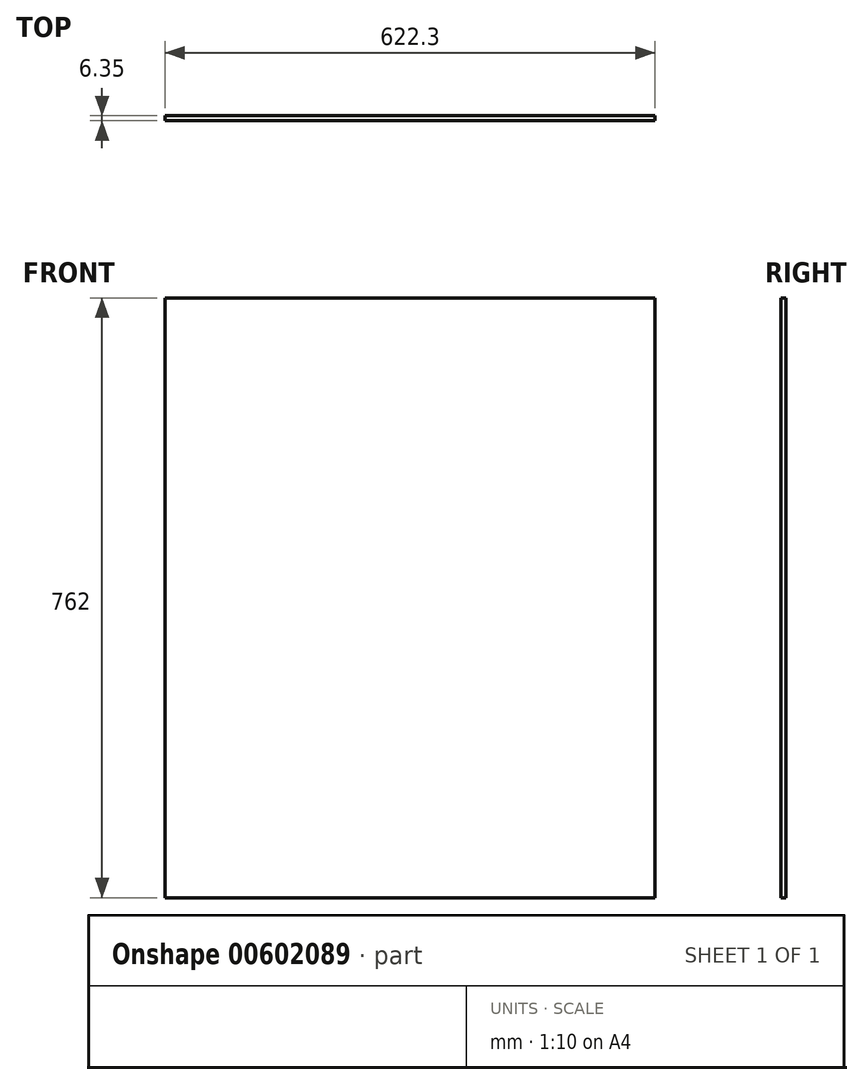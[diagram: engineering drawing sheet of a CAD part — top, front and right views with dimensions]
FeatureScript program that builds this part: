
annotation { "Feature Type Name" : "Feature", "Feature Type Description" : "" }
export const myFeature = defineFeature(function(context is Context, id is Id, definition is map)
    precondition{}
    {
        {
            var Q0;
            Q0=qCreatedBy(makeId("Front.planeOp"),FACE);
            var sketch = newSketch(context, id + "F0", { "sketchPlane" : qUnion([Q0])});
            skLineSegment(sketch, "E0.bottom", {"start": v(311.15, 381) * mm, "end": v(-311.15, 381) * mm});
            skLineSegment(sketch, "E0.top", {"start": v(311.15, -381) * mm, "end": v(-311.15, -381) * mm});
            skLineSegment(sketch, "E0.left", {"start": v(311.15, 381) * mm, "end": v(311.15, -381) * mm});
            skLineSegment(sketch, "E0.right", {"start": v(-311.15, 381) * mm, "end": v(-311.15, -381) * mm});
            skPoint(sketch, "E0.middle", {"position": v(0, 0) * mm});
            skSolve(sketch);
        }
        {
            var Q0;
            Q0=makeQuery(id+"F0.imprint","IMPRINT",FACE,{"disambiguationData":[TD([[makeQuery(id+"F0.imprint","IMPRINT",EDGE,{"derivedFrom":sQuery(id+"F0.wireOp",EDGE,"E0.bottom")}),1.0]])]});
            extrude(context, id + "F1", {"entities" : qUnion([Q0]), "depth" : 6.35 * mm, "offsetDistance" : 25.4 * mm});
        }
    });
